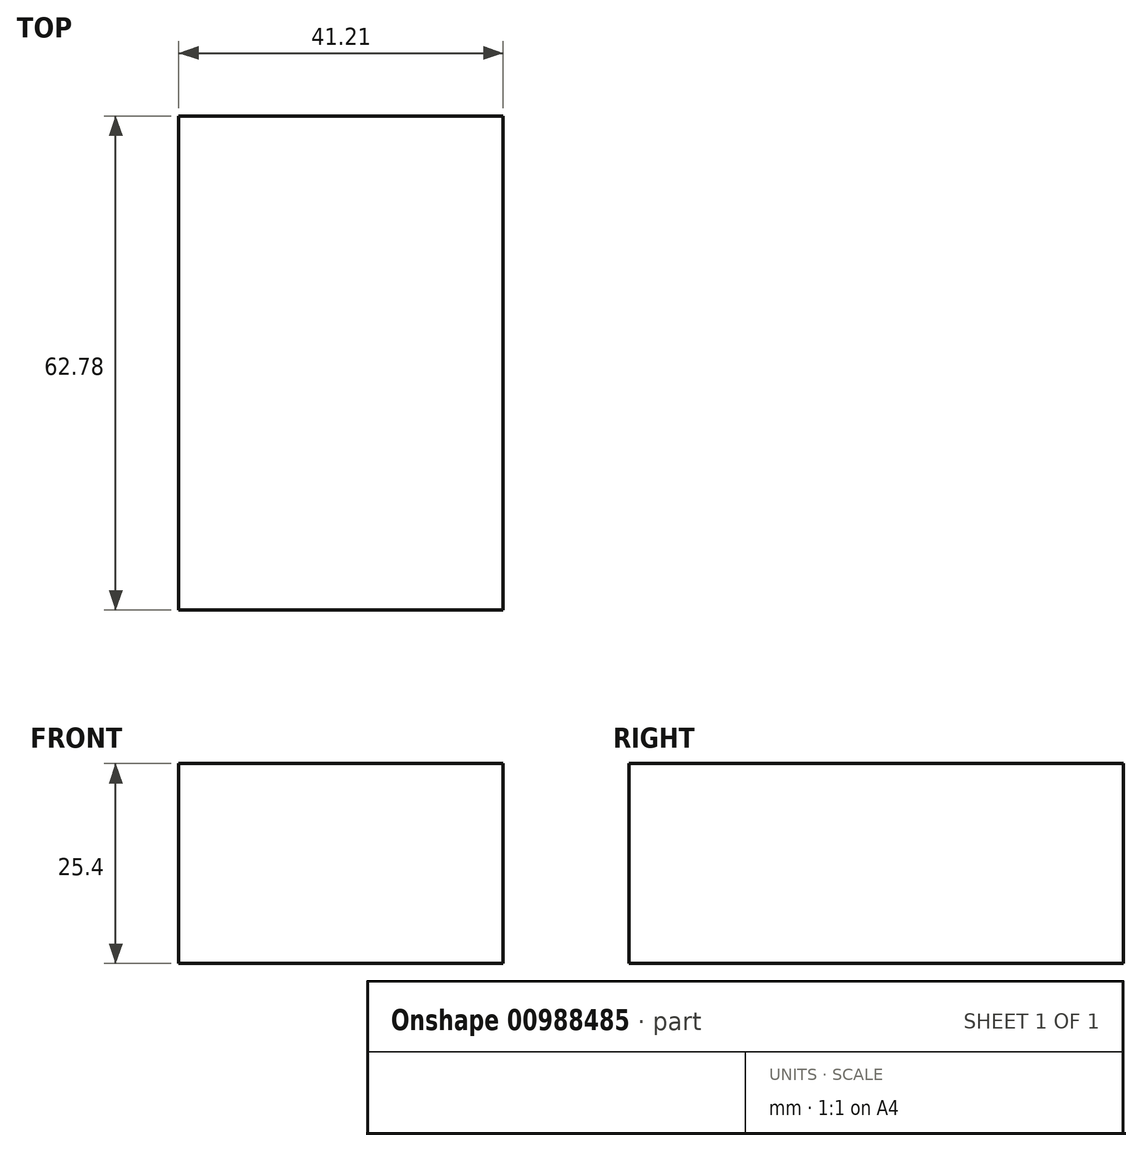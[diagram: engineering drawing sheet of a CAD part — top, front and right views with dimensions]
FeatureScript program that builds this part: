
annotation { "Feature Type Name" : "Feature", "Feature Type Description" : "" }
export const myFeature = defineFeature(function(context is Context, id is Id, definition is map)
    precondition{}
    {
        {
            var Q0;
            Q0=qCreatedBy(makeId("Top.planeOp"),FACE);
            var sketch = newSketch(context, id + "F0", { "sketchPlane" : qUnion([Q0])});
            skLineSegment(sketch, "E0.bottom", {"start": v(-21.17, 35.98) * mm, "end": v(20.04, 35.98) * mm});
            skLineSegment(sketch, "E0.top", {"start": v(-21.17, -26.8) * mm, "end": v(20.04, -26.8) * mm});
            skLineSegment(sketch, "E0.left", {"start": v(-21.17, 35.98) * mm, "end": v(-21.17, -26.8) * mm});
            skLineSegment(sketch, "E0.right", {"start": v(20.04, 35.98) * mm, "end": v(20.04, -26.8) * mm});
            skSolve(sketch);
        }
        {
            var Q0;
            Q0=makeQuery(id+"F0.imprint","IMPRINT",FACE,{"disambiguationData":[TD([[makeQuery(id+"F0.imprint","IMPRINT",EDGE,{"derivedFrom":sQuery(id+"F0.wireOp",EDGE,"E0.bottom")}),-1.0]])]});
            extrude(context, id + "F1", {"entities" : qUnion([Q0]), "depth" : 25.4 * mm, "offsetDistance" : 25.4 * mm});
        }
    });
